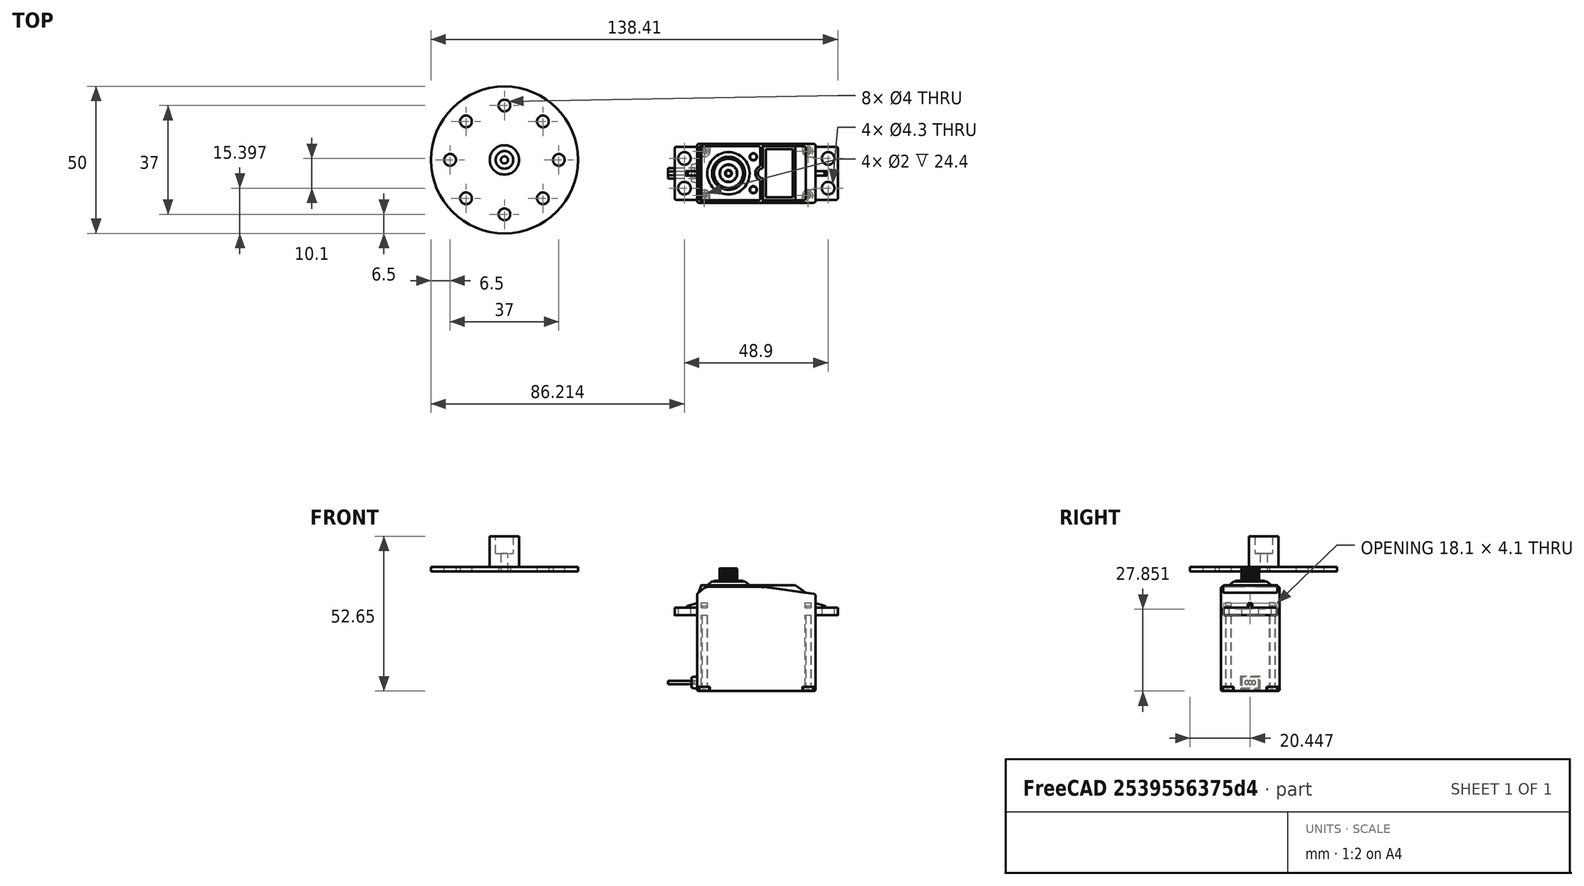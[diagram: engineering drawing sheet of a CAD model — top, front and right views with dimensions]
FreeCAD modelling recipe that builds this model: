
FCSTD DOCUMENT  (FreeCAD 0.20R29177 +426 (Git))
Label: rotor
License: All rights reserved
LicenseURL: http://en.wikipedia.org/wiki/All_rights_reserved
objects: Part::Cylinder×11, Part::MultiFuse×3, Part::Feature×1, Sketcher::SketchObject×1, Part::Extrusion×1, Part::Cut×1
note: 18 computed .brp shape members not serialized (recipe doc carries the construction recipe); baked Part::Feature solids carry a one-line shape summary decoded from their .brp

FEATURE [Part::Cylinder] cylinder
  Angle = 360
  AttacherType = Attacher::AttachEngine3D
  FirstAngle = 0
  Height = 1.5
  Radius = 25
  SecondAngle = 0
FEATURE [Part::Cylinder] cylinder002
  Angle = 360
  AttacherType = Attacher::AttachEngine3D
  FirstAngle = 0
  Height = 5
  Placement = pos=(18.5,0,0) rot=(0,0,1;0rad)
  Radius = 2
  SecondAngle = 0
FEATURE [Part::Cylinder] cylinder003
  Angle = 360
  AttacherType = Attacher::AttachEngine3D
  FirstAngle = 0
  Height = 5
  Placement = pos=(13.0815,13.0815,0) rot=(0,0,1;0.785398rad)
  Radius = 2
  SecondAngle = 0
FEATURE [Part::Cylinder] cylinder004
  Angle = 360
  AttacherType = Attacher::AttachEngine3D
  FirstAngle = 0
  Height = 5
  Placement = pos=(0,18.5,0) rot=(0,0,1;1.5708rad)
  Radius = 2
  SecondAngle = 0
FEATURE [Part::Cylinder] cylinder005
  Angle = 360
  AttacherType = Attacher::AttachEngine3D
  FirstAngle = 0
  Height = 5
  Placement = pos=(-13.0815,13.0815,0) rot=(0,0,1;2.35619rad)
  Radius = 2
  SecondAngle = 0
FEATURE [Part::Cylinder] cylinder006
  Angle = 360
  AttacherType = Attacher::AttachEngine3D
  FirstAngle = 0
  Height = 5
  Placement = pos=(-18.5,2e-15,0) rot=(0,0,1;3.14159rad)
  Radius = 2
  SecondAngle = 0
FEATURE [Part::Cylinder] cylinder007
  Angle = 360
  AttacherType = Attacher::AttachEngine3D
  FirstAngle = 0
  Height = 5
  Placement = pos=(-13.0815,-13.0815,0) rot=(0,0,1;3.92699rad)
  Radius = 2
  SecondAngle = 0
FEATURE [Part::Cylinder] cylinder008
  Angle = 360
  AttacherType = Attacher::AttachEngine3D
  FirstAngle = 0
  Height = 5
  Placement = pos=(0,-18.5,0) rot=(0,0,-1;1.5708rad)
  Radius = 2
  SecondAngle = 0
FEATURE [Part::Cylinder] cylinder009
  Angle = 360
  AttacherType = Attacher::AttachEngine3D
  FirstAngle = 0
  Height = 5
  Placement = pos=(13.0815,-13.0815,0) rot=(0,0,-1;0.785398rad)
  Radius = 2
  SecondAngle = 0
FEATURE [Part::MultiFuse] Group
  Placement = pos=(0,0,-1) rot=(0,0,1;0rad)
  Shapes = -> [cylinder002,cylinder003,cylinder004,cylinder005,cylinder006,cylinder007,cylinder008,cylinder009]
FEATURE [Part::Feature] Shape001
  Placement = pos=(85.6641,-4.55315,-40.6487) rot=(0,0,1;3.14159rad)
  shape: bbox 57.75 x 20 x 41.74 mm, 378 faces, 4 solids (baked)
FEATURE [Part::Cylinder] cylinder010  label="servo_central_shaft"
  Angle = 360
  AttacherType = Attacher::AttachEngine3D
  FirstAngle = 0
  Height = 12
  Radius = 5
  SecondAngle = 0
FEATURE [Sketcher::SketchObject] Sketch
  FullyConstrained = false
  MapMode = 5
  Placement = pos=(85.6641,-4.55315,1.09128) rot=(0,0,1;3.14159rad)
  Support = -> [Shape001]
  sketch-geometry (1):
    g0: Circle CenterX=9.4502 CenterY=-0.000218 CenterZ=0 NormalX=0 NormalY=0 NormalZ=1 AngleXU=0 Radius=3
  constraints (1):
    c: Radius(g0) = 3
FEATURE [Part::Extrusion] Extrude
  Base = -> Sketch
  Dir = (0,0,1)
  DirMode = 2
  FaceMakerClass = Part::FaceMakerBullseye
  LengthFwd = 9
  LengthRev = 0
  Placement = pos=(-76.21,4.55,5) rot=(0,0,1;0rad)
  Solid = true
  Symmetric = false
FEATURE [Part::Cylinder] Cylinder
  Angle = 360
  AttacherType = Attacher::AttachEngine3D
  FirstAngle = 0
  Height = 19
  Placement = pos=(0,0,-1) rot=(0,0,1;0rad)
  Radius = 1.2
  SecondAngle = 0
FEATURE [Part::MultiFuse] Fusion
  Shapes = -> [Group,Extrude,Cylinder]
FEATURE [Part::MultiFuse] Fusion001
  Shapes = -> [cylinder,cylinder010]
FEATURE [Part::Cut] Cut  label="rotor"
  Base = -> Fusion001
  Tool = -> Fusion
